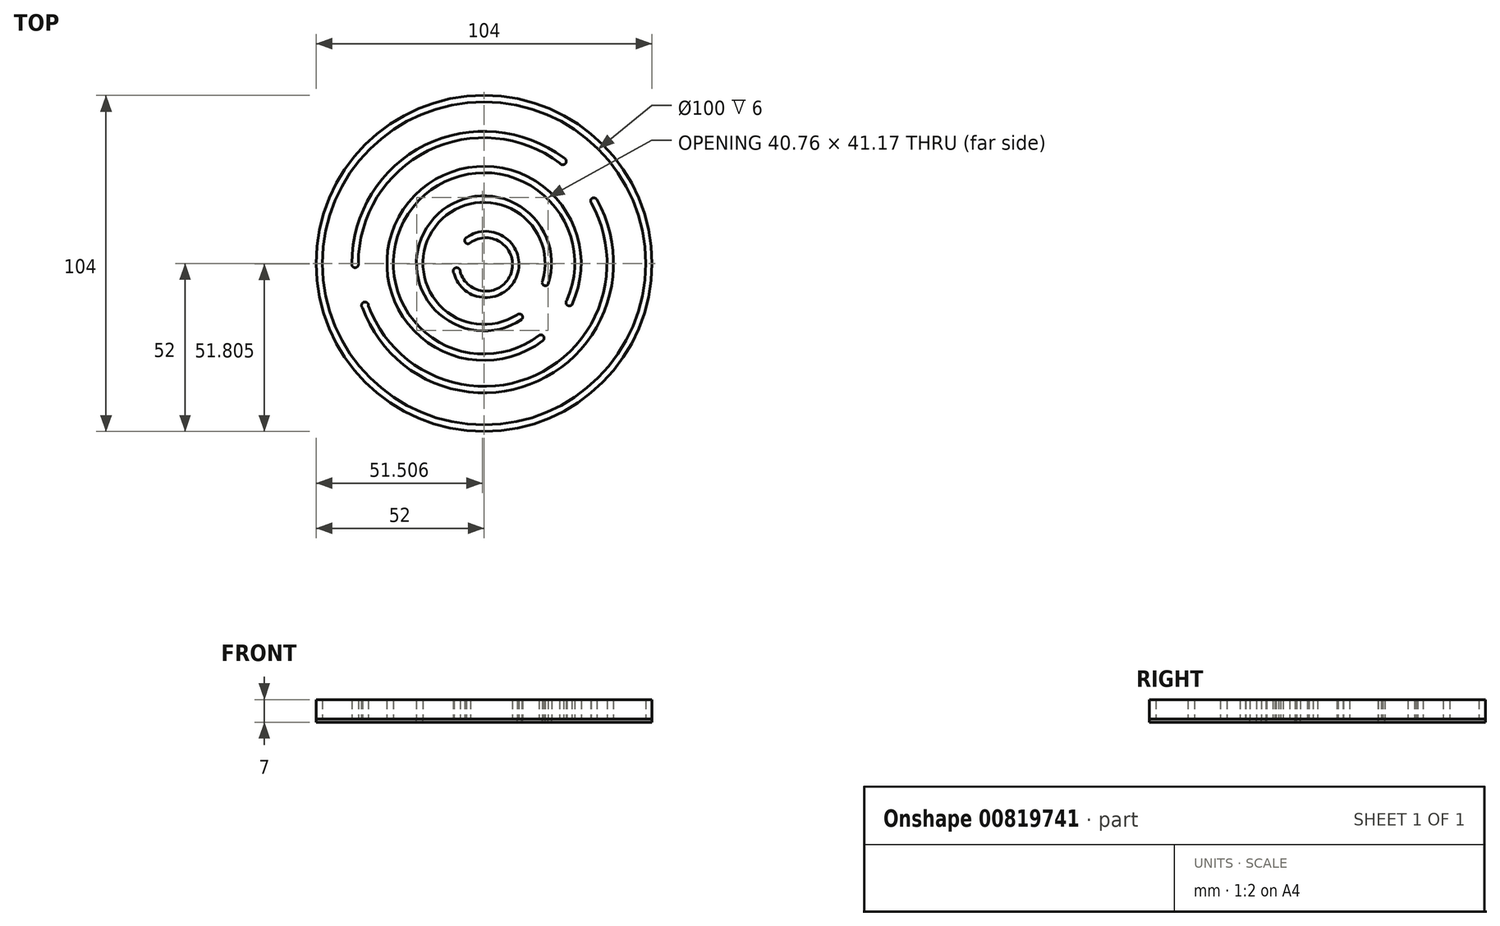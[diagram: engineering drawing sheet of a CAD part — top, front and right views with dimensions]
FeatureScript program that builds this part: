
annotation { "Feature Type Name" : "Feature", "Feature Type Description" : "" }
export const myFeature = defineFeature(function(context is Context, id is Id, definition is map)
    precondition{}
    {
        {
            var Q0;
            Q0=qCreatedBy(makeId("Top.planeOp"),FACE);
            var sketch = newSketch(context, id + "F0", { "sketchPlane" : qUnion([Q0])});
            skCircle(sketch, "E0", {"center": v(0, 0) * mm, "radius": 50 * mm});
            skArc(sketch, "E1", {"start": v(0, 38.9) * mm, "mid": v(-27.5, 27.5) * mm, "end": v(-38.9, 0) * mm});
            skArc(sketch, "E2", {"start": v(-35.75, -13.07) * mm, "mid": v(-21.81, -31.2) * mm, "end": v(0, -38.07) * mm});
            skArc(sketch, "E3", {"start": v(0, -38.07) * mm, "mid": v(26.92, -26.92) * mm, "end": v(38.07, 0) * mm});
            skArc(sketch, "E4", {"start": v(23.42, 31.06) * mm, "mid": v(12.35, 36.9) * mm, "end": v(0, 38.9) * mm});
            skArc(sketch, "E5", {"start": v(38.07, 0) * mm, "mid": v(36.82, 9.68) * mm, "end": v(33.14, 18.73) * mm});
            skArc(sketch, "E6", {"start": v(0, 30.05) * mm, "mid": v(-21.25, 21.25) * mm, "end": v(-30.05, 0) * mm});
            skArc(sketch, "E7", {"start": v(-30.05, 0) * mm, "mid": v(-21.25, -21.25) * mm, "end": v(0, -30.05) * mm});
            skArc(sketch, "E8", {"start": v(0, -30.05) * mm, "mid": v(9.57, -28.49) * mm, "end": v(18.15, -23.95) * mm});
            skArc(sketch, "E9", {"start": v(27.18, -12.82) * mm, "mid": v(29.32, -6.57) * mm, "end": v(30.05, 0) * mm});
            skArc(sketch, "E10", {"start": v(30.05, 0) * mm, "mid": v(21.25, 21.25) * mm, "end": v(0, 30.05) * mm});
            skArc(sketch, "E11", {"start": v(18.15, -5.3) * mm, "mid": v(-15.16, 11.3) * mm, "end": v(10.26, -15.88) * mm});
            skArc(sketch, "E12", {"start": v(-9.32, -3.09) * mm, "mid": v(10.22, -3.75) * mm, "end": v(-5.4, 8) * mm});
            skArc(sketch, "E13.0", {"start": v(19.88, -6.46) * mm, "mid": v(-16.7, 12.58) * mm, "end": v(11.69, -17.34) * mm});
            skArc(sketch, "E14.0", {"start": v(-7.4, -2.55) * mm, "mid": v(8.34, -3.08) * mm, "end": v(-4.24, 6.38) * mm});
            skArc(sketch, "E15.0", {"start": v(0, 28.05) * mm, "mid": v(-19.83, 19.83) * mm, "end": v(-28.05, 0) * mm});
            skArc(sketch, "E16.0", {"start": v(-28.05, 0) * mm, "mid": v(-19.83, -19.83) * mm, "end": v(0, -28.05) * mm});
            skArc(sketch, "E17.0", {"start": v(0, -28.05) * mm, "mid": v(8.97, -26.58) * mm, "end": v(16.99, -22.32) * mm});
            skArc(sketch, "E18.0", {"start": v(25.64, -11.37) * mm, "mid": v(27.44, -5.81) * mm, "end": v(28.05, 0) * mm});
            skArc(sketch, "E19.0", {"start": v(28.05, 0) * mm, "mid": v(19.83, 19.83) * mm, "end": v(0, 28.05) * mm});
            skArc(sketch, "E20.0", {"start": v(0, 40.9) * mm, "mid": v(-28.92, 28.92) * mm, "end": v(-40.9, 0) * mm});
            skArc(sketch, "E21.0", {"start": v(24.62, 32.66) * mm, "mid": v(12.98, 38.79) * mm, "end": v(0, 40.9) * mm});
            skArc(sketch, "E22.0", {"start": v(40.07, 0) * mm, "mid": v(38.75, 10.2) * mm, "end": v(34.88, 19.72) * mm});
            skArc(sketch, "E23.0", {"start": v(0, -40.07) * mm, "mid": v(28.33, -28.33) * mm, "end": v(40.07, 0) * mm});
            skArc(sketch, "E24.0", {"start": v(-37.63, -13.76) * mm, "mid": v(-22.96, -32.84) * mm, "end": v(0, -40.07) * mm});
            skCircle(sketch, "E25.0", {"center": v(0, 0) * mm, "radius": 52 * mm});
            skArc(sketch, "E26", {"start": v(-35.75, -13.07) * mm, "mid": v(-37.2, -12.02) * mm, "end": v(-37.63, -13.76) * mm});
            skArc(sketch, "E27", {"start": v(-40.9, 0) * mm, "mid": v(-39.9, -1.32) * mm, "end": v(-38.9, 0) * mm});
            skArc(sketch, "E28", {"start": v(-7.4, -2.55) * mm, "mid": v(-8.76, -1.39) * mm, "end": v(-9.32, -3.09) * mm});
            skArc(sketch, "E29", {"start": v(-5.4, 8) * mm, "mid": v(-5.8, 6.5) * mm, "end": v(-4.24, 6.38) * mm});
            skArc(sketch, "E30", {"start": v(34.88, 19.72) * mm, "mid": v(33.48, 20.17) * mm, "end": v(33.14, 18.73) * mm});
            skArc(sketch, "E31", {"start": v(23.42, 31.06) * mm, "mid": v(25.23, 30.95) * mm, "end": v(24.62, 32.66) * mm});
            skArc(sketch, "E32", {"start": v(18.15, -5.3) * mm, "mid": v(18.44, -6.74) * mm, "end": v(19.88, -6.46) * mm});
            skArc(sketch, "E33", {"start": v(25.64, -11.37) * mm, "mid": v(25.67, -12.88) * mm, "end": v(27.18, -12.82) * mm});
            skArc(sketch, "E34", {"start": v(11.69, -17.34) * mm, "mid": v(11.67, -15.93) * mm, "end": v(10.26, -15.88) * mm});
            skArc(sketch, "E35", {"start": v(18.15, -23.95) * mm, "mid": v(18.4, -22.55) * mm, "end": v(16.99, -22.32) * mm});
            skSolve(sketch);
        }
        {
            var Q0;
            Q0 = qSketchRegion(id + "F0", true);
            var Q1;
            Q1=makeQuery(id+"F0.imprint","IMPRINT",FACE,{"disambiguationData":[TD([[makeQuery(id+"F0.imprint","IMPRINT",EDGE,{"derivedFrom":sQuery(id+"F0.wireOp",EDGE,"E1")}),-1.0]])]});
            var Q2;
            Q2=makeQuery(id+"F0.imprint","IMPRINT",FACE,{"disambiguationData":[TD([[makeQuery(id+"F0.imprint","IMPRINT",EDGE,{"derivedFrom":sQuery(id+"F0.wireOp",EDGE,"E6")}),1.0]])]});
            var Q3;
            Q3=makeQuery(id+"F0.imprint","IMPRINT",FACE,{"disambiguationData":[TD([[makeQuery(id+"F0.imprint","IMPRINT",EDGE,{"derivedFrom":sQuery(id+"F0.wireOp",EDGE,"E11")}),-1.0]])]});
            var Q4;
            Q4=makeQuery(id+"F0.imprint","IMPRINT",FACE,{"disambiguationData":[TD([[makeQuery(id+"F0.imprint","IMPRINT",EDGE,{"derivedFrom":sQuery(id+"F0.wireOp",EDGE,"E12")}),1.0]])]});
            var Q5;
            Q5=makeQuery(id+"F0.imprint","IMPRINT",FACE,{"disambiguationData":[TD([[makeQuery(id+"F0.imprint","IMPRINT",EDGE,{"derivedFrom":sQuery(id+"F0.wireOp",EDGE,"E2")}),-1.0]])]});
            extrude(context, id + "F1", {"entities" : qUnion([Q0, Q1, Q2, Q3, Q4, Q5]), "depth" : 6 * mm, "offsetDistance" : 25 * mm});
        }
        {
            var Q0;
            Q0=qCreatedBy(makeId("Top.planeOp"),FACE);
            var sketch = newSketch(context, id + "F2", { "sketchPlane" : qUnion([Q0])});
            skCircle(sketch, "E36.0", {"center": v(0, 0) * mm, "radius": 52 * mm});
            skArc(sketch, "E37.0", {"start": v(24.62, 32.66) * mm, "mid": v(-18.25, 36.6) * mm, "end": v(-40.9, 0) * mm});
            skArc(sketch, "E38.0", {"start": v(27.18, -12.82) * mm, "mid": v(-23.34, 18.93) * mm, "end": v(18.15, -23.95) * mm});
            skArc(sketch, "E39.0", {"start": v(19.88, -6.46) * mm, "mid": v(-16.7, 12.58) * mm, "end": v(11.69, -17.34) * mm});
            skArc(sketch, "E40.0.0", {"start": v(18.15, -5.3) * mm, "mid": v(18.44, -6.74) * mm, "end": v(19.88, -6.46) * mm});
            skArc(sketch, "E40.0.2", {"start": v(11.69, -17.34) * mm, "mid": v(11.67, -15.93) * mm, "end": v(10.26, -15.88) * mm});
            skArc(sketch, "E40.0.3", {"start": v(10.26, -15.88) * mm, "mid": v(-15.16, 11.3) * mm, "end": v(18.15, -5.3) * mm});
            skArc(sketch, "E41.0", {"start": v(-9.32, -3.09) * mm, "mid": v(10.22, -3.75) * mm, "end": v(-5.4, 8) * mm});
            skArc(sketch, "E42.0", {"start": v(-37.63, -13.76) * mm, "mid": v(16.8, -36.38) * mm, "end": v(34.88, 19.72) * mm});
            skSolve(sketch);
        }
        {
            var Q0;
            Q0 = qSketchRegion(id + "F2", true);
            extrude(context, id + "F3", {"entities" : qUnion([Q0]), "oppositeDirection" : true, "depth" : 1 * mm, "offsetDistance" : 25 * mm});
        }
    });
